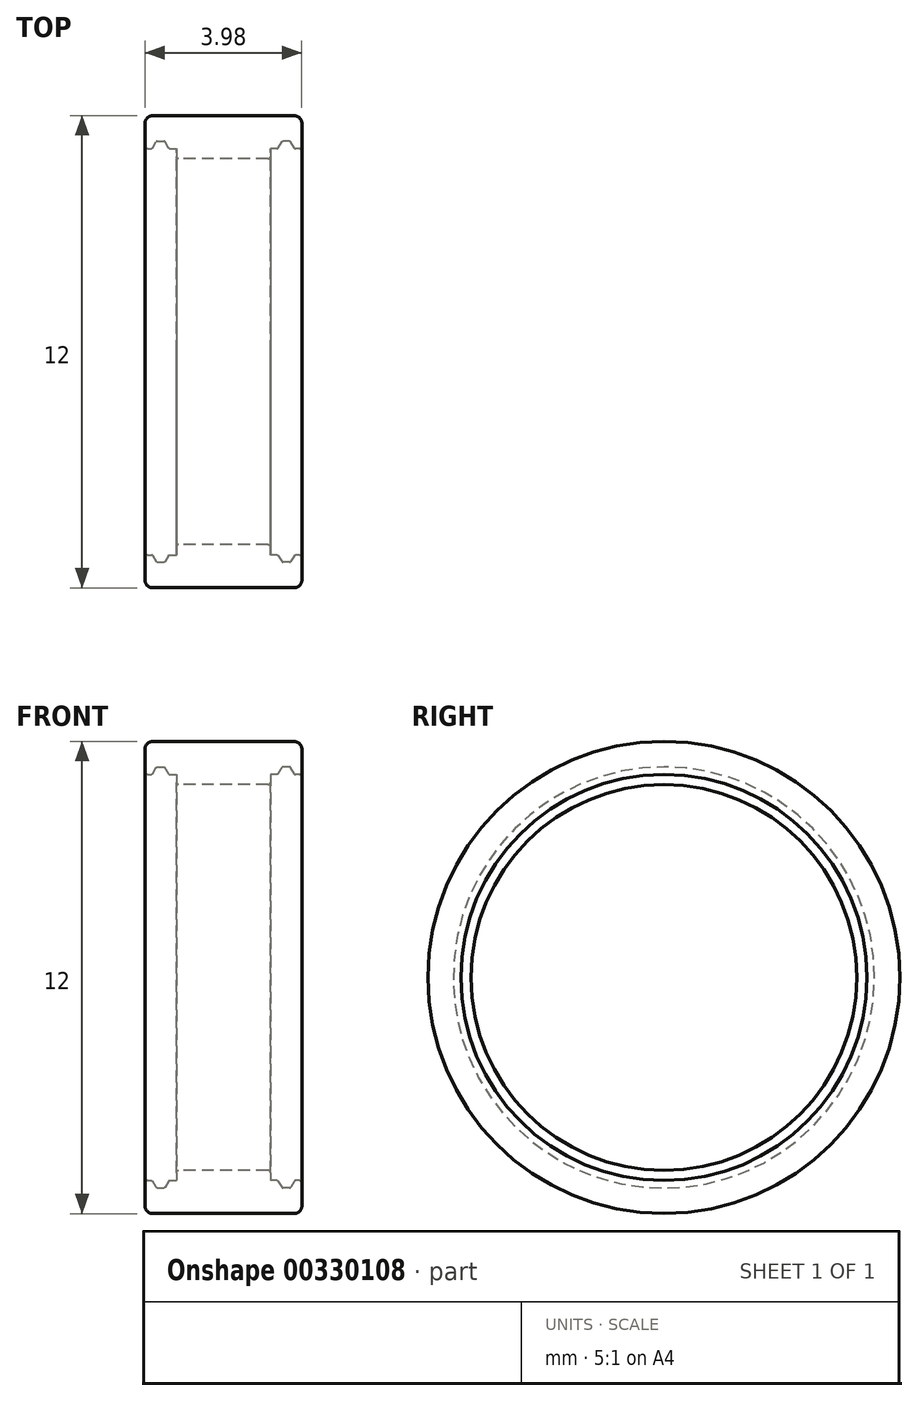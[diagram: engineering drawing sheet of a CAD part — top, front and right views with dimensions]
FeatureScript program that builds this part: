
annotation { "Feature Type Name" : "Feature", "Feature Type Description" : "" }
export const myFeature = defineFeature(function(context is Context, id is Id, definition is map)
    precondition{}
    {
        {
            var Q0;
            Q0=qCreatedBy(makeId("Front.planeOp"),FACE);
            var sketch = newSketch(context, id + "F0", { "sketchPlane" : qUnion([Q0])});
            skLineSegment(sketch, "E0", {"start": v(0, 0) * mm, "end": v(2, 0) * mm});
            skLineSegment(sketch, "E1", {"start": v(0, 6) * mm, "end": v(2, 6) * mm});
            skLineSegment(sketch, "E2", {"start": v(1.81, 5.16) * mm, "end": v(2, 5.16) * mm});
            skLineSegment(sketch, "E3", {"start": v(1.6, 5.35) * mm, "end": v(1.7, 5.35) * mm});
            skLineSegment(sketch, "E4", {"start": v(1.7, 5.35) * mm, "end": v(1.6, 5.35) * mm});
            skLineSegment(sketch, "E5", {"start": v(1.6, 5.35) * mm, "end": v(1.5, 5.35) * mm});
            skLineSegment(sketch, "E6", {"start": v(1.7, 5.35) * mm, "end": v(1.81, 5.16) * mm});
            skLineSegment(sketch, "E7", {"start": v(1.2, 5.16) * mm, "end": v(1.2, 4.9) * mm});
            skLineSegment(sketch, "E8", {"start": v(1.2, 4.9) * mm, "end": v(0, 4.9) * mm});
            skLineSegment(sketch, "E9", {"start": v(1.2, 5.16) * mm, "end": v(1.38, 5.16) * mm});
            skLineSegment(sketch, "E10", {"start": v(1.38, 5.16) * mm, "end": v(1.5, 5.35) * mm});
            skLineSegment(sketch, "E11", {"start": v(2, 5.16) * mm, "end": v(2, 6) * mm});
            skLineSegment(sketch, "E12", {"start": v(0, 6) * mm, "end": v(0, 4.9) * mm});
            skLineSegment(sketch, "E13", {"start": v(1.5, 5.35) * mm, "end": v(1.38, 5.35) * mm});
            skSolve(sketch);
        }
        {
            var Q0;
            Q0=makeQuery(id+"F0.imprint","IMPRINT",FACE,{"disambiguationData":[TD([[makeQuery(id+"F0.imprint","IMPRINT",EDGE,{"derivedFrom":sQuery(id+"F0.wireOp",EDGE,"E1")}),-1.0]])]});
            var Q1;
            Q1=sQuery(id+"F0.wireOp",EDGE,"E0");
            revolve(context, id + "F1", {"entities" : qUnion([Q0]), "axis" : qUnion([Q1]), "revolveType" : RevolveType.FULL});
        }
        {
            var Q0;
            Q0=makeQuery(id+"F1.opRevolve","SWEPT_EDGE",EDGE,{"disambiguationData":[OSD([sQuery(id+"F0.wireOp",EDGE,"E2"),sQuery(id+"F0.wireOp",EDGE,"E11")])]});
            fillet(context, id + "F2", {"entities" : qUnion([Q0]), "radius" : 0.06 * mm, "tangentPropagation" : true, "allowEdgeOverflow" : false});
        }
        {
            var Q0;
            Q0=makeQuery(id+"F1.opRevolve","SWEPT_EDGE",EDGE,{"disambiguationData":[OSD([sQuery(id+"F0.wireOp",EDGE,"E9"),sQuery(id+"F0.wireOp",EDGE,"E10")])]});
            var Q1;
            Q1=makeQuery(id+"F1.opRevolve","SWEPT_EDGE",EDGE,{"disambiguationData":[OSD([sQuery(id+"F0.wireOp",EDGE,"E5"),sQuery(id+"F0.wireOp",EDGE,"E10")])]});
            var Q2;
            Q2=makeQuery(id+"F1.opRevolve","SWEPT_EDGE",EDGE,{"disambiguationData":[OSD([sQuery(id+"F0.wireOp",EDGE,"E4"),sQuery(id+"F0.wireOp",EDGE,"E6")])]});
            var Q3;
            Q3=makeQuery(id+"F1.opRevolve","SWEPT_EDGE",EDGE,{"disambiguationData":[OSD([sQuery(id+"F0.wireOp",EDGE,"E2"),sQuery(id+"F0.wireOp",EDGE,"E6")])]});
            fillet(context, id + "F3", {"entities" : qUnion([Q0, Q1, Q2, Q3]), "radius" : 0.03 * mm, "tangentPropagation" : true, "allowEdgeOverflow" : false});
        }
        {
            var Q0;
            Q0=makeQuery(id+"F1.opRevolve","SWEPT_EDGE",EDGE,{"disambiguationData":[OSD([sQuery(id+"F0.wireOp",EDGE,"E7"),sQuery(id+"F0.wireOp",EDGE,"E8")])]});
            fillet(context, id + "F4", {"entities" : qUnion([Q0]), "radius" : 0.06 * mm, "tangentPropagation" : true, "allowEdgeOverflow" : false});
        }
        {
            var Q0;
            Q0=makeQuery(id+"F1.opRevolve","SWEPT_EDGE",EDGE,{"disambiguationData":[OSD([sQuery(id+"F0.wireOp",EDGE,"E1"),sQuery(id+"F0.wireOp",EDGE,"E11")])]});
            fillet(context, id + "F5", {"entities" : qUnion([Q0]), "radius" : 0.2 * mm, "tangentPropagation" : true, "allowEdgeOverflow" : false});
        }
        {
            var Q0;
            Q0=makeQuery(id+"F1.opRevolve","SWEPT_BODY",BODY,{"disambiguationData":[OSD([sQuery(id+"F0.wireOp",EDGE,"E1"),sQuery(id+"F0.wireOp",EDGE,"E2"),sQuery(id+"F0.wireOp",EDGE,"E4"),sQuery(id+"F0.wireOp",EDGE,"E5"),sQuery(id+"F0.wireOp",EDGE,"E6"),sQuery(id+"F0.wireOp",EDGE,"E7"),sQuery(id+"F0.wireOp",EDGE,"E8"),sQuery(id+"F0.wireOp",EDGE,"E9"),sQuery(id+"F0.wireOp",EDGE,"E10"),sQuery(id+"F0.wireOp",EDGE,"E11"),sQuery(id+"F0.wireOp",EDGE,"E12")])]});
            var Q1;
            Q1=qCreatedBy(makeId("Right.planeOp"),FACE);
            mirror(context, id + "F6", {"operationType" : NewBodyOperationType.ADD, "entities" : qUnion([Q0]), "mirrorPlane" : qUnion([Q1])});
        }
    });
